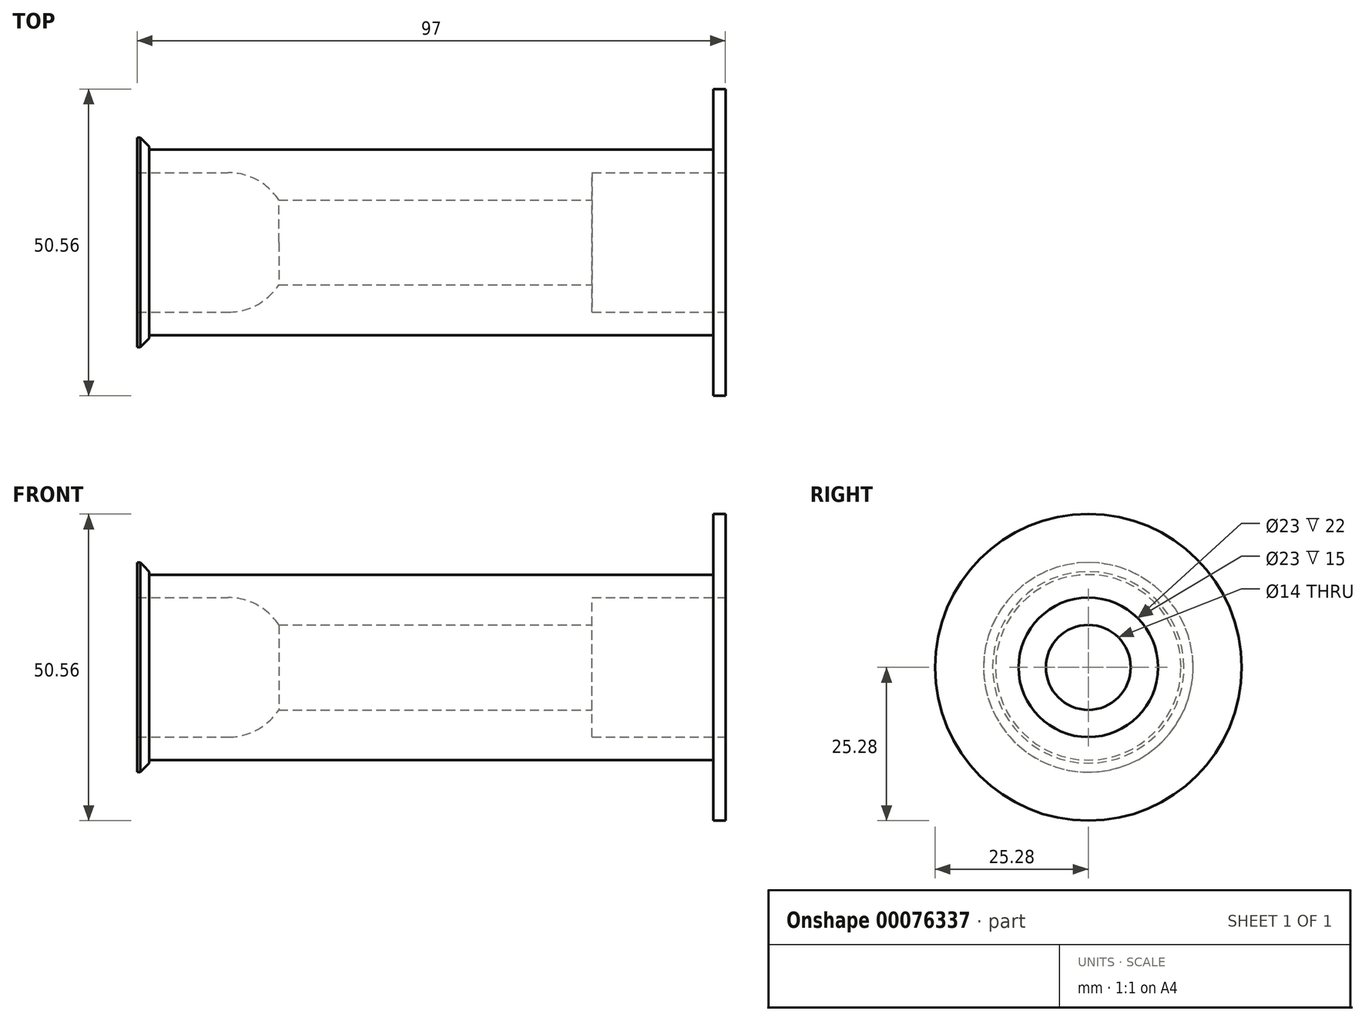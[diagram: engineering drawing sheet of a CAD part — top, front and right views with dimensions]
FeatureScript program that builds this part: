
annotation { "Feature Type Name" : "Feature", "Feature Type Description" : "" }
export const myFeature = defineFeature(function(context is Context, id is Id, definition is map)
    precondition{}
    {
        {
            var Q0;
            Q0=qCreatedBy(makeId("Top.planeOp"),FACE);
            var sketch = newSketch(context, id + "F0", { "sketchPlane" : qUnion([Q0])});
            skLineSegment(sketch, "E0", {"start": v(-46.49, 0) * mm, "end": v(54.32, 0) * mm, "construction": true});
            skLineSegment(sketch, "E1", {"start": v(31.9, 0) * mm, "end": v(-18.38, 0) * mm});
            skLineSegment(sketch, "E2", {"start": v(-18.38, 0) * mm, "end": v(-18.38, 1.5) * mm});
            skLineSegment(sketch, "E3", {"start": v(-28.38, 11.5) * mm, "end": v(-43.38, 11.5) * mm});
            skLineSegment(sketch, "E4", {"start": v(-43.38, 11.5) * mm, "end": v(-43.38, 15.28) * mm});
            skLineSegment(sketch, "E5", {"start": v(-41.38, 15.28) * mm, "end": v(39.62, 15.28) * mm});
            skLineSegment(sketch, "E6", {"start": v(53.62, 11.5) * mm, "end": v(31.62, 11.5) * mm});
            skLineSegment(sketch, "E7", {"start": v(31.62, 11.5) * mm, "end": v(31.62, 0) * mm});
            skLineSegment(sketch, "E8", {"start": v(31.62, 0) * mm, "end": v(-18.38, 0) * mm});
            skLineSegment(sketch, "E9.bottom", {"start": v(-43.38, 15.28) * mm, "end": v(-43.38, 15.28) * mm});
            skLineSegment(sketch, "E9.top", {"start": v(-43.38, 17.28) * mm, "end": v(-43.38, 17.28) * mm});
            skLineSegment(sketch, "E9.left", {"start": v(-43.38, 15.28) * mm, "end": v(-43.38, 17.28) * mm});
            skLineSegment(sketch, "E9.right", {"start": v(-43.38, 15.28) * mm, "end": v(-43.38, 17.28) * mm});
            skLineSegment(sketch, "E10", {"start": v(-43.38, 17.28) * mm, "end": v(-41.38, 17.28) * mm});
            skLineSegment(sketch, "E11", {"start": v(-41.38, 17.28) * mm, "end": v(-41.38, 15.28) * mm});
            skPoint(sketch, "E12.visualSharp", {"position": v(-18.38, 11.5) * mm});
            skArc(sketch, "E12.filletArc", {"start": v(-18.38, 1.5) * mm, "mid": v(-21.3, 8.57) * mm, "end": v(-28.38, 11.5) * mm});
            skLineSegment(sketch, "E13", {"start": v(39.62, 15.28) * mm, "end": v(51.62, 15.28) * mm});
            skLineSegment(sketch, "E14", {"start": v(53.62, 15.28) * mm, "end": v(53.62, 11.5) * mm});
            skLineSegment(sketch, "E15", {"start": v(51.62, 15.28) * mm, "end": v(51.62, 25.28) * mm});
            skLineSegment(sketch, "E16", {"start": v(51.62, 25.28) * mm, "end": v(53.62, 25.28) * mm});
            skLineSegment(sketch, "E17", {"start": v(53.62, 25.28) * mm, "end": v(53.62, 15.28) * mm});
            skSolve(sketch);
        }
        {
            var Q0;
            {var subQ0=sQuery(id+"F0.wireOp",EDGE,"E2");Q0=makeQuery(id+"F0.imprint","IMPRINT",FACE,{"disambiguationData":[TD([[makeQuery(id+"F0.imprint","IMPRINT",EDGE,{"derivedFrom":subQ0}),-1.0]])]});}
            var Q1;
            Q1=sQuery(id+"F0.wireOp",EDGE,"E8");
            revolve(context, id + "F1", {"entities" : qUnion([Q0]), "axis" : qUnion([Q1]), "revolveType" : RevolveType.FULL});
        }
        {
            var Q0;
            Q0=makeQuery(id+"F1.opRevolve","SWEPT_EDGE",EDGE,{"disambiguationData":[OSD([sQuery(id+"F0.wireOp",EDGE,"E10"),sQuery(id+"F0.wireOp",EDGE,"E11")])]});
            var Q1;
            Q1=makeQuery(id+"F1.opRevolve","SWEPT_EDGE",EDGE,{"disambiguationData":[OSD([sQuery(id+"F0.wireOp",EDGE,"BICERwqB-TdZt-SLDO-KyFK-9c4IbI52pTiZ.top"),sQuery(id+"F0.wireOp",EDGE,"BICERwqB-TdZt-SLDO-KyFK-9c4IbI52pTiZ.right")])]});
            chamfer(context, id + "F2", {"entities" : qUnion([Q0, Q1]), "width" : 1.5 * mm, "tangentPropagation" : true});
        }
        {
            var Q0;
            Q0=makeQuery(id+"F1.opRevolve","SWEPT_FACE",FACE,{"disambiguationData":[OSD([sQuery(id+"F0.wireOp",EDGE,"E7")])]});
            var sketch = newSketch(context, id + "F3", { "sketchPlane" : qUnion([Q0])});
            skCircle(sketch, "E18", {"center": v(0, 0) * mm, "radius": 7 * mm});
            skSolve(sketch);
        }
        {
            var Q0;
            Q0 = qSketchRegion(id + "F3", true);
            extrude(context, id + "F4", {"entities" : qUnion([Q0]), "operationType" : NewBodyOperationType.REMOVE, "endBound" : BoundingType.THROUGH_ALL, "oppositeDirection" : true, "depth" : 25 * mm});
        }
    });
